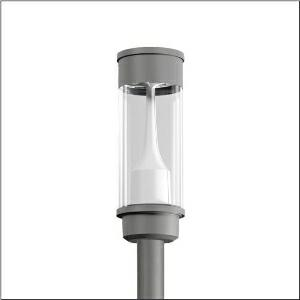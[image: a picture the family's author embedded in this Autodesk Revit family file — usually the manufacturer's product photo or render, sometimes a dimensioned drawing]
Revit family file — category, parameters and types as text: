
# Revit family: litepole_iq___pl1_2s_5xa5415cf14h_d917
name_source: partatom
category: Lighting Fixtures
units: mm (PartAtom-declared; Revit-internal decimal feet)

## family parameters
Cut with Voids When Loaded = No
Host = Face
Light Source = No
Part Type = Normal
Room Calculation Point = No
Round Connector Dimension = Use Diameter
Shared = No

## types (1)
- --- (1 x LED, 2970 lm, 23.9 W, 2200K)
    Apparent Load = 24 VA
    CIE Flux Codes = 23 62 94 96 100
    Color Rendering = 70
    Color Temperature = 2200K
    Default Elevation = 1800 mm
    Description = Litepole iQ, mast luminaire, Module 540 iQ-SR, primary light control with 3 zone facetted reflector, of plastic, silver coated, highly specular, structured, primary optical cover: cover, of PMMA, transparent, partly coated, light distribution: PL1.2s, light emission: direct distribution, primary light characteristic: symmetric, installation type: post-top, LED, High Power LED, rated luminous flux: 2.970lm, luminous efficacy: 124lm/W, light colour: 722, colour temperature: 2200K, control gear: iQ Street-Remote, control: optimised constant luminous flux control (CLO 2.0), Desk-Remote (wireless, voltage-free reading and setting of iQ features in the workshop via application-optimized NFC function/RFID function), Light-Fading, Smart-Wire, Night-Set, Lumen-Switch, Temp-Guard, Auto-Match, Street-Remote, pre-setting: logarithmic dimming characteristic, with terminal, 6-pole, max. 2.5mm², mains connection: 230..240V, AC, 50/60Hz, start of lifetime: 24W, end of service life: 26W, reduction: 12W, luminaire housing, upper part, of glass-fibre reinforced polyester, coated, Siteco® metallic grey (DB 702S), diameter: 210mm, height: 590mm, spigot size: d x l = 76 x 70mm (post-top) | with reducer (optional accessory) 60 x 70mm, mounting height: 3..5m, post-top mast mounting element, of diecast aluminium, coated, Siteco® metallic grey (DB 702S), Module 540 iQ-SR, traffic white (RAL 9016), equipment: standard, protection rating (complete): IP65, insulation class (complete): insulation class II (safety insulation), certification: CE, ENEC, VDE, packaging unit: 1 piece

Light Distribution: PL1.2s
    Height = 590 mm
    Lamp = 1 x LED
    Lamp Light Flux = 2970 lm
    Lamp Power = 23.9 W
    Lamp count = 1
    Length = 220 mm
    Luminous efficacy = 124 lm/W
    Manufacturer = Siteco
    ModVariant = No
    Model = 5XA5415CF14H
    Number of Poles = 1
    OnlyDefault = Yes
    Power Factor = 1
    Product Name = Litepole iQ | PL1.2s
    Product group = mast luminaire | pylon top
    ProductGroupID = 6100
    Protection Class = Protection class II
    Protection Degree = IP 65
    RLX_Detail_Level = 1
    RLX_Emergency_Light_Flux = 0 lm
    RLX_Emergency_Type = 0
    RLX_Emergency_Type_DB = No
    RlxData = <blob elided: 25133 chars, md5=f673c53f>
    Socket = socket
    Standby Power = 0 W
    System Light Flux = 2970 lm
    System Power = 24 W
    Type Comments = factory setting: luminous flux: 100 % | dim-lin: 254 | 499 mA
    Type Image = l_1006025.jpg
    URL = http://relux.com
    VarID = @adj_166343
    Voltage = 0 V
    Weight = 0.00 kg
    Width = 0 mm  [stored 0 ft]

note: [stored X ft] marks values corroborated as IEEE doubles in the binary element streams (Revit-internal decimal feet)

## geometry (parser evidence)
native form markers: Blend x4, Sweep x11
no freeform markers — native parametric forms only
